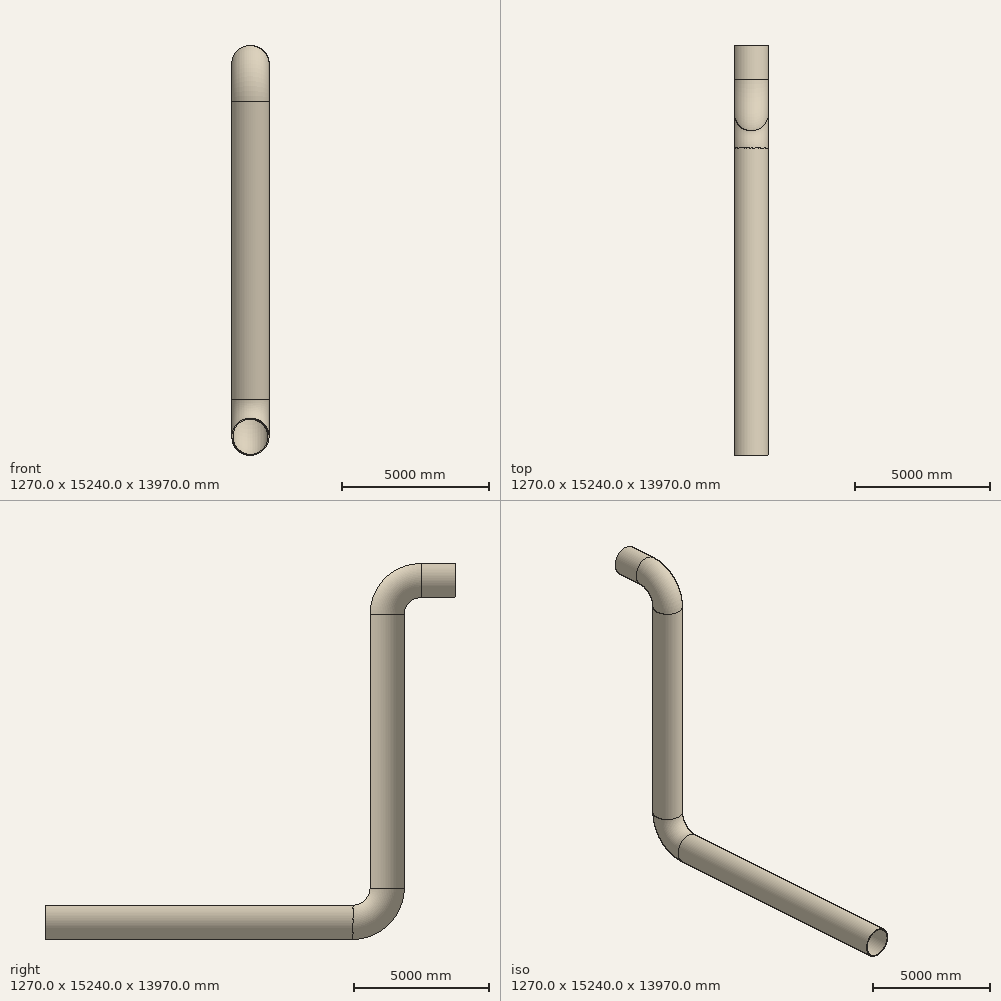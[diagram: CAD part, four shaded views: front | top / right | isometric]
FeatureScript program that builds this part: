
annotation { "Feature Type Name" : "Feature", "Feature Type Description" : "" }
export const myFeature = defineFeature(function(context is Context, id is Id, definition is map)
    precondition{}
    {
        {
            var Q0;
            Q0=qCreatedBy(makeId("Front.planeOp"),FACE);
            var sketch = newSketch(context, id + "F0", { "sketchPlane" : qUnion([Q0])});
            skCircle(sketch, "E0", {"center": v(0, 0) * mm, "radius": 635 * mm});
            skCircle(sketch, "E1", {"center": v(0, 0) * mm, "radius": 596.9 * mm});
            skSolve(sketch);
        }
        {
            var Q0;
            Q0=qCreatedBy(makeId("Right.planeOp"),FACE);
            var sketch = newSketch(context, id + "F1", { "sketchPlane" : qUnion([Q0])});
            skLineSegment(sketch, "E2", {"start": v(0, 0) * mm, "end": v(-1270, 0) * mm});
            skLineSegment(sketch, "E3", {"start": v(-2540, -1270) * mm, "end": v(-2540, -11430) * mm});
            skLineSegment(sketch, "E4", {"start": v(-3810, -12700) * mm, "end": v(-15240, -12700) * mm});
            skPoint(sketch, "E5.visualSharp", {"position": v(-2540, 0) * mm});
            skArc(sketch, "E5.filletArc", {"start": v(-1270, 0) * mm, "mid": v(-2168.03, -371.97) * mm, "end": v(-2540, -1270) * mm});
            skPoint(sketch, "E6.visualSharp", {"position": v(-2540, -12700) * mm});
            skArc(sketch, "E6.filletArc", {"start": v(-3810, -12700) * mm, "mid": v(-2911.97, -12328.03) * mm, "end": v(-2540, -11430) * mm});
            skSolve(sketch);
        }
        {
            var Q0;
            Q0=makeQuery(id+"F0.imprint","IMPRINT",FACE,{"disambiguationData":[TD([[makeQuery(id+"F0.imprint","IMPRINT",EDGE,{"derivedFrom":sQuery(id+"F0.wireOp",EDGE,"E0")}),1.0]])]});
            var Q1;
            Q1=sQuery(id+"F1.wireOp",EDGE,"E2");
            var Q2;
            Q2=sQuery(id+"F1.wireOp",EDGE,"E5.filletArc");
            var Q3;
            Q3=sQuery(id+"F1.wireOp",EDGE,"E3");
            var Q4;
            Q4=sQuery(id+"F1.wireOp",EDGE,"E6.filletArc");
            var Q5;
            Q5=sQuery(id+"F1.wireOp",EDGE,"E4");
            sweep(context, id + "F2", {"profiles" : qUnion([Q0]), "path" : qUnion([Q1, Q2, Q3, Q4, Q5])});
        }
    });
